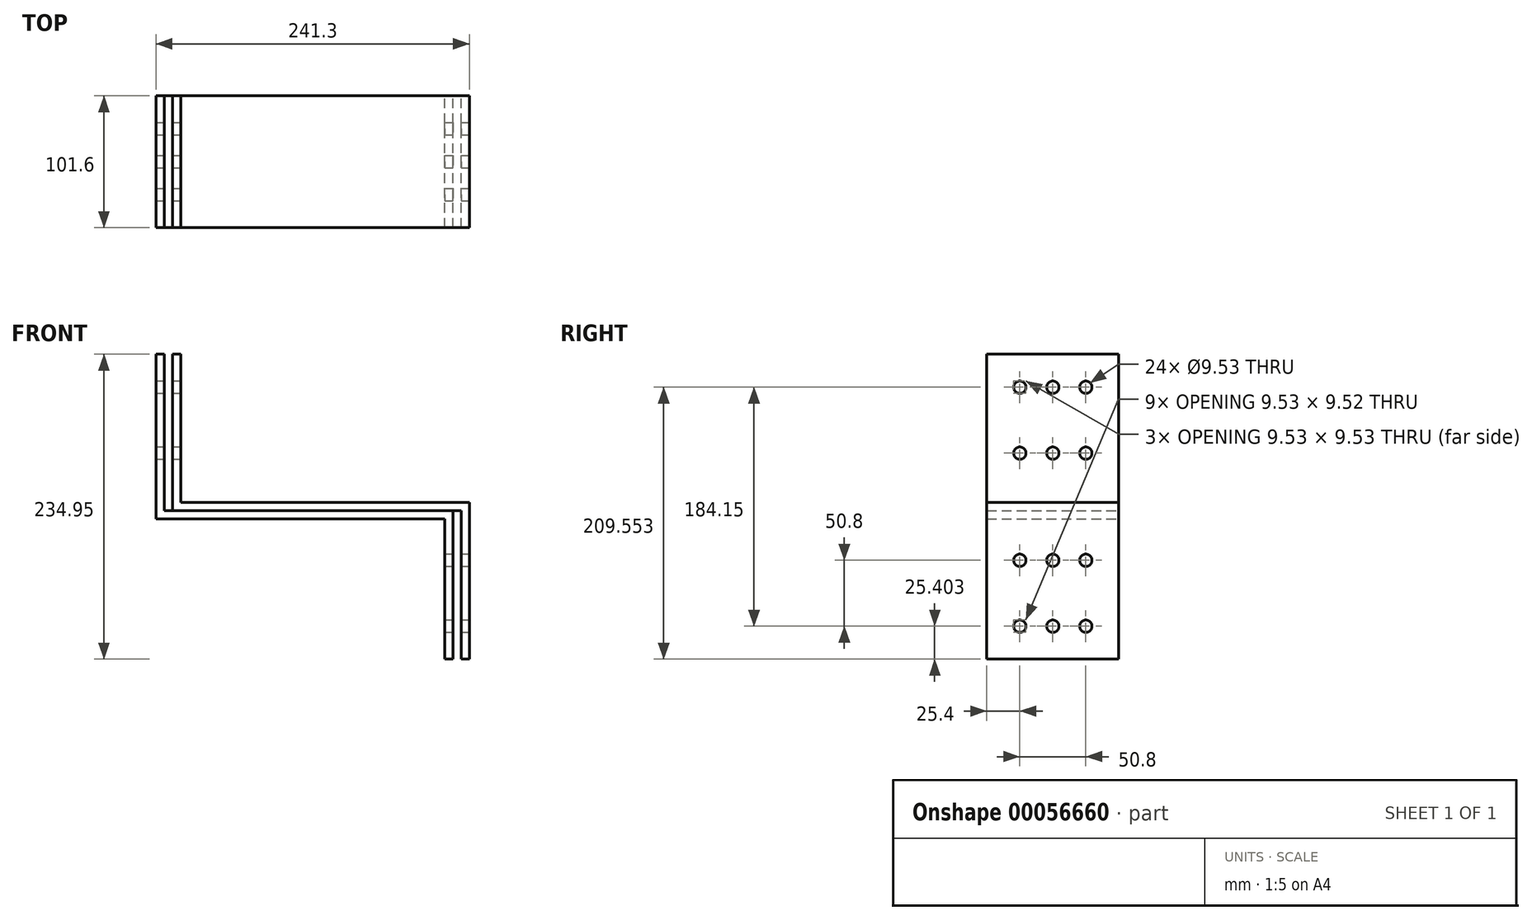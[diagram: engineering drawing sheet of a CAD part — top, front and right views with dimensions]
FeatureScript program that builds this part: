
annotation { "Feature Type Name" : "Feature", "Feature Type Description" : "" }
export const myFeature = defineFeature(function(context is Context, id is Id, definition is map)
    precondition{}
    {
        {
            var Q0;
            Q0=qCreatedBy(makeId("Front.planeOp"),FACE);
            var sketch = newSketch(context, id + "F0", { "sketchPlane" : qUnion([Q0])});
            skLineSegment(sketch, "E0", {"start": v(101.97, -102.5) * mm, "end": v(101.97, 5.44) * mm});
            skLineSegment(sketch, "E1", {"start": v(101.97, 5.44) * mm, "end": v(-120.28, 5.44) * mm});
            skLineSegment(sketch, "E2", {"start": v(-120.28, 5.44) * mm, "end": v(-120.28, 132.44) * mm});
            skLineSegment(sketch, "E3", {"start": v(-113.93, 11.8) * mm, "end": v(108.32, 11.8) * mm});
            skLineSegment(sketch, "E4.trimOffspring", {"start": v(-113.93, 132.44) * mm, "end": v(-113.93, 11.8) * mm});
            skLineSegment(sketch, "E5", {"start": v(108.32, 11.8) * mm, "end": v(108.32, -102.5) * mm});
            skLineSegment(sketch, "E6", {"start": v(108.32, -102.5) * mm, "end": v(101.97, -102.5) * mm});
            skLineSegment(sketch, "E7", {"start": v(-113.93, 132.44) * mm, "end": v(-120.28, 132.44) * mm});
            skSolve(sketch);
        }
        {
            var Q0;
            Q0=qSketchRegion(id+"F0",true);
            extrude(context, id + "F1", {"entities" : qUnion([Q0]), "endBound" : BoundingType.SYMMETRIC, "depth" : 101.6 * mm});
        }
        {
            var Q0;
            Q0=qCreatedBy(makeId("Front.planeOp"),FACE);
            var sketch = newSketch(context, id + "F2", { "sketchPlane" : qUnion([Q0])});
            skLineSegment(sketch, "E8", {"start": v(114.67, -102.5) * mm, "end": v(114.67, 11.8) * mm});
            skLineSegment(sketch, "E9", {"start": v(114.67, 11.8) * mm, "end": v(-107.58, 11.8) * mm});
            skLineSegment(sketch, "E10", {"start": v(-107.58, 11.8) * mm, "end": v(-107.58, 132.44) * mm});
            skLineSegment(sketch, "E11", {"start": v(-101.23, 18.14) * mm, "end": v(121.02, 18.14) * mm});
            skLineSegment(sketch, "E12.trimOffspring", {"start": v(-101.23, 132.44) * mm, "end": v(-101.23, 18.14) * mm});
            skLineSegment(sketch, "E13", {"start": v(121.02, 18.14) * mm, "end": v(121.02, -102.5) * mm});
            skLineSegment(sketch, "E14", {"start": v(121.02, -102.5) * mm, "end": v(114.67, -102.5) * mm});
            skLineSegment(sketch, "E15", {"start": v(-101.23, 132.44) * mm, "end": v(-107.58, 132.44) * mm});
            skSolve(sketch);
        }
        {
            var Q0;
            Q0=qSketchRegion(id+"F2",true);
            extrude(context, id + "F3", {"entities" : qUnion([Q0]), "endBound" : BoundingType.SYMMETRIC, "depth" : 101.6 * mm});
        }
        {
            var Q0;
            Q0=makeQuery(id+"F3.opExtrude","SWEPT_FACE",FACE,{"disambiguationData":[OSD([sQuery(id+"F2.wireOp",EDGE,"E13")])]});
            var sketch = newSketch(context, id + "F4", { "sketchPlane" : qUnion([Q0])});
            skCircle(sketch, "E16", {"center": v(-25.4, -77.1) * mm, "radius": 4.76 * mm});
            skCircle(sketch, "E17", {"center": v(-25.4, 107.04) * mm, "radius": 4.76 * mm});
            skCircle(sketch, "E18.0.1.0", {"center": v(-25.4, 56.24) * mm, "radius": 4.76 * mm});
            skCircle(sketch, "E18.1.0.0", {"center": v(0, 107.04) * mm, "radius": 4.76 * mm});
            skCircle(sketch, "E18.1.1.0", {"center": v(0, 56.24) * mm, "radius": 4.76 * mm});
            skCircle(sketch, "E18.2.0.0", {"center": v(25.4, 107.04) * mm, "radius": 4.76 * mm});
            skCircle(sketch, "E18.2.1.0", {"center": v(25.4, 56.24) * mm, "radius": 4.76 * mm});
            skLineSegment(sketch, "E18.direction1", {"start": v(-25.4, 107.04) * mm, "end": v(0, 107.04) * mm, "construction": true});
            skLineSegment(sketch, "E18.direction2", {"start": v(-25.4, 107.04) * mm, "end": v(-25.4, 56.24) * mm, "construction": true});
            skCircle(sketch, "E19.0.1.0", {"center": v(-25.4, -26.3) * mm, "radius": 4.76 * mm});
            skCircle(sketch, "E19.1.0.0", {"center": v(0, -77.1) * mm, "radius": 4.76 * mm});
            skCircle(sketch, "E19.1.1.0", {"center": v(0, -26.3) * mm, "radius": 4.76 * mm});
            skCircle(sketch, "E19.2.0.0", {"center": v(25.4, -77.1) * mm, "radius": 4.76 * mm});
            skCircle(sketch, "E19.2.1.0", {"center": v(25.4, -26.3) * mm, "radius": 4.76 * mm});
            skLineSegment(sketch, "E19.direction1", {"start": v(-25.4, -77.1) * mm, "end": v(0, -77.1) * mm, "construction": true});
            skLineSegment(sketch, "E19.direction2", {"start": v(-25.4, -77.1) * mm, "end": v(-25.4, -26.3) * mm, "construction": true});
            skSolve(sketch);
        }
        {
            var Q0;
            Q0=qSketchRegion(id+"F4",true);
            extrude(context, id + "F5", {"entities" : qUnion([Q0]), "operationType" : NewBodyOperationType.REMOVE, "endBound" : BoundingType.THROUGH_ALL, "oppositeDirection" : true, "depth" : 25.4 * mm});
        }
    });
